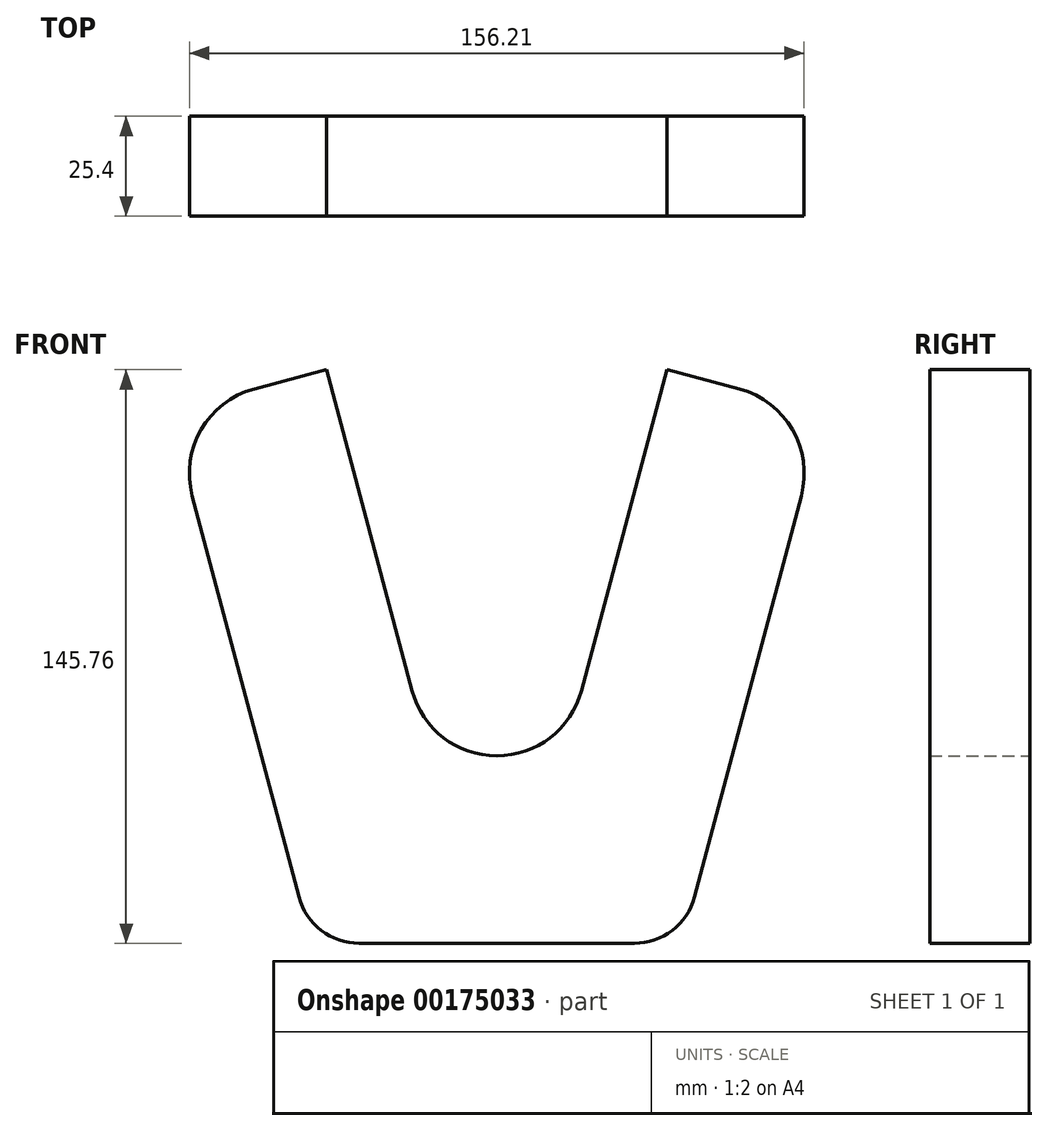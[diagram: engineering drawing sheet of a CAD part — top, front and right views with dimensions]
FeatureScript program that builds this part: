
annotation { "Feature Type Name" : "Feature", "Feature Type Description" : "" }
export const myFeature = defineFeature(function(context is Context, id is Id, definition is map)
    precondition{}
    {
        {
            var Q0;
            Q0=qCreatedBy(makeId("Front.planeOp"),FACE);
            var sketch = newSketch(context, id + "F0", { "sketchPlane" : qUnion([Q0])});
            skCircle(sketch, "E0", {"center": v(-111.76, 33.9) * mm, "radius": 22.23 * mm});
            skCircle(sketch, "E1", {"center": v(0, 33.9) * mm, "radius": 22.23 * mm});
            skCircle(sketch, "E2", {"center": v(-55.88, -15.63) * mm, "radius": 22.23 * mm});
            skCircle(sketch, "E3", {"center": v(-20.96, -69.6) * mm, "radius": 15.88 * mm});
            skCircle(sketch, "E4", {"center": v(-90.8, -69.6) * mm, "radius": 15.88 * mm});
            skLineSegment(sketch, "E5", {"start": v(-117.47, 55.38) * mm, "end": v(-99.06, 60.28) * mm});
            skLineSegment(sketch, "E6", {"start": v(21.48, 28.2) * mm, "end": v(-5.61, -73.68) * mm});
            skLineSegment(sketch, "E7", {"start": v(-20.95, -85.48) * mm, "end": v(-90.8, -85.48) * mm});
            skLineSegment(sketch, "E8", {"start": v(-133.24, 28.2) * mm, "end": v(-106.15, -73.68) * mm});
            skPoint(sketch, "E9", {"position": v(-55.88, -85.48) * mm});
            skLineSegment(sketch, "E10", {"start": v(-12.7, 60.28) * mm, "end": v(5.71, 55.38) * mm});
            skLineSegment(sketch, "E11", {"start": v(-99.06, 60.28) * mm, "end": v(-77.36, -21.34) * mm});
            skLineSegment(sketch, "E12", {"start": v(-12.7, 60.28) * mm, "end": v(-34.4, -21.34) * mm});
            skSolve(sketch);
        }
        {
            var Q0;
            {var subQ0=sQuery(id+"F0.wireOp",EDGE,"E5");var subQ1=sQuery(id+"F0.wireOp",EDGE,"E0");var subQ2=makeQuery(id+"F0.imprint","INTERSECT",VERTEX,{"disambiguationData":[OD(1.0)],"derivedFrom":[subQ1,subQ0]});Q0=makeQuery(id+"F0.imprint","IMPRINT",FACE,{"disambiguationData":[TD([[makeQuery(id+"F0.imprint","IMPRINT",EDGE,{"disambiguationData":[TD([[subQ2,1.0]])],"derivedFrom":subQ1}),-1.0]])]});}
            var Q1;
            {var subQ0=sQuery(id+"F0.wireOp",EDGE,"E5");var subQ1=sQuery(id+"F0.wireOp",EDGE,"E0");var subQ2=makeQuery(id+"F0.imprint","INTERSECT",VERTEX,{"disambiguationData":[OD(0.0)],"derivedFrom":[subQ1,subQ0]});Q1=makeQuery(id+"F0.imprint","IMPRINT",FACE,{"disambiguationData":[TD([[makeQuery(id+"F0.imprint","IMPRINT",EDGE,{"disambiguationData":[TD([[subQ2,1.0]])],"derivedFrom":subQ1}),1.0]])]});}
            var Q2;
            {var subQ0=sQuery(id+"F0.wireOp",EDGE,"E10");Q2=makeQuery(id+"F0.imprint","IMPRINT",FACE,{"disambiguationData":[TD([[makeQuery(id+"F0.imprint","IMPRINT",EDGE,{"derivedFrom":subQ0}),1.0]])]});}
            var Q3;
            {var subQ0=sQuery(id+"F0.wireOp",EDGE,"E6");var subQ1=sQuery(id+"F0.wireOp",EDGE,"E1");var subQ2=makeQuery(id+"F0.imprint","INTERSECT",VERTEX,{"disambiguationData":[OD(0.0)],"derivedFrom":[subQ1,subQ0]});Q3=makeQuery(id+"F0.imprint","IMPRINT",FACE,{"disambiguationData":[TD([[makeQuery(id+"F0.imprint","IMPRINT",EDGE,{"disambiguationData":[TD([[subQ2,1.0]])],"derivedFrom":subQ1}),1.0]])]});}
            var Q4;
            {var subQ0=sQuery(id+"F0.wireOp",EDGE,"E4");var subQ1=makeQuery(id+"F0.imprint","INTERSECT",VERTEX,{"derivedFrom":[subQ0,sQuery(id+"F0.wireOp",EDGE,"E7")]});Q4=makeQuery(id+"F0.imprint","IMPRINT",FACE,{"disambiguationData":[TD([[makeQuery(id+"F0.imprint","IMPRINT",EDGE,{"disambiguationData":[TD([[subQ1,1.0]])],"derivedFrom":subQ0}),1.0]])]});}
            var Q5;
            {var subQ0=sQuery(id+"F0.wireOp",EDGE,"E3");var subQ1=makeQuery(id+"F0.imprint","INTERSECT",VERTEX,{"derivedFrom":[subQ0,sQuery(id+"F0.wireOp",EDGE,"E6")]});Q5=makeQuery(id+"F0.imprint","IMPRINT",FACE,{"disambiguationData":[TD([[makeQuery(id+"F0.imprint","IMPRINT",EDGE,{"disambiguationData":[TD([[subQ1,1.0]])],"derivedFrom":subQ0}),1.0]])]});}
            var Q6;
            {var subQ0=sQuery(id+"F0.wireOp",EDGE,"E5");var subQ1=sQuery(id+"F0.wireOp",EDGE,"E0");var subQ3=makeQuery(id+"F0.imprint","INTERSECT",VERTEX,{"disambiguationData":[OD(1.0)],"derivedFrom":[subQ1,subQ0]});Q6=makeQuery(id+"F0.imprint","IMPRINT",FACE,{"disambiguationData":[TD([[makeQuery(id+"F0.imprint","IMPRINT",EDGE,{"disambiguationData":[TD([[subQ3,1.0]])],"derivedFrom":subQ1}),1.0]])]});}
            var Q7;
            {var subQ1=sQuery(id+"F0.wireOp",EDGE,"E1");var subQ3=sQuery(id+"F0.wireOp",EDGE,"E6");var subQ5=makeQuery(id+"F0.imprint","INTERSECT",VERTEX,{"disambiguationData":[OD(0.0)],"derivedFrom":[subQ1,subQ3]});Q7=makeQuery(id+"F0.imprint","IMPRINT",FACE,{"disambiguationData":[TD([[makeQuery(id+"F0.imprint","IMPRINT",EDGE,{"disambiguationData":[TD([[subQ5,-1.0]])],"derivedFrom":subQ1}),1.0]])]});}
            var Q8;
            {var subQ17=sQuery(id+"F0.wireOp",EDGE,"E8");Q8=makeQuery(id+"F0.imprint","IMPRINT",FACE,{"disambiguationData":[TD([[makeQuery(id+"F0.imprint","IMPRINT",EDGE,{"derivedFrom":subQ17}),1.0]])]});}
            var Q9;
            {var subQ0=sQuery(id+"F0.wireOp",EDGE,"E10");Q9=makeQuery(id+"F0.imprint","IMPRINT",FACE,{"disambiguationData":[TD([[makeQuery(id+"F0.imprint","IMPRINT",EDGE,{"derivedFrom":subQ0}),-1.0]])]});}
            extrude(context, id + "F1", {"entities" : qUnion([Q0, Q1, Q2, Q3, Q4, Q5, Q6, Q7, Q8, Q9]), "depth" : 25.4 * mm});
        }
    });
